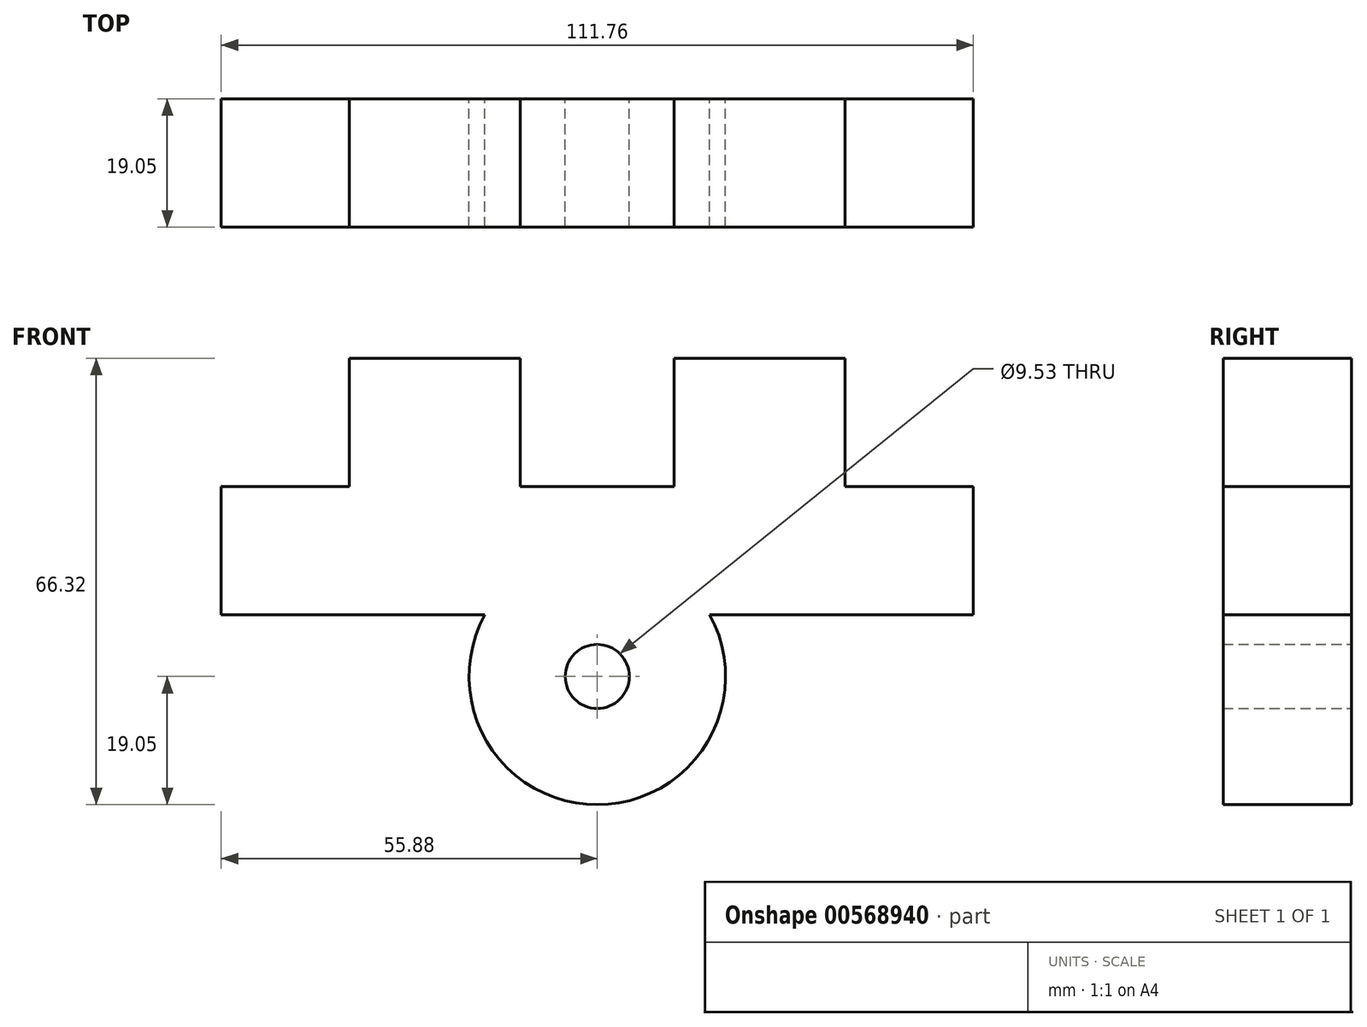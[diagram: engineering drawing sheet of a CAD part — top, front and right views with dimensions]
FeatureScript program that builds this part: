
annotation { "Feature Type Name" : "Feature", "Feature Type Description" : "" }
export const myFeature = defineFeature(function(context is Context, id is Id, definition is map)
    precondition{}
    {
        {
            var Q0;
            Q0=qCreatedBy(makeId("Front.planeOp"),FACE);
            var sketch = newSketch(context, id + "F0", { "sketchPlane" : qUnion([Q0])});
            skCircle(sketch, "E0", {"center": v(0, 0) * mm, "radius": 19.05 * mm});
            skLineSegment(sketch, "E1", {"start": v(0, 0) * mm, "end": v(0, 19.05) * mm});
            skCircle(sketch, "E2", {"center": v(0, 0) * mm, "radius": 4.76 * mm});
            skLineSegment(sketch, "E3.bottom", {"start": v(-55.88, 28.22) * mm, "end": v(55.88, 28.22) * mm});
            skLineSegment(sketch, "E3.top", {"start": v(-55.88, 9.17) * mm, "end": v(55.88, 9.17) * mm});
            skLineSegment(sketch, "E3.left", {"start": v(-55.88, 28.22) * mm, "end": v(-55.88, 9.17) * mm});
            skLineSegment(sketch, "E3.right", {"start": v(55.88, 28.22) * mm, "end": v(55.88, 9.17) * mm});
            skLineSegment(sketch, "E4.bottom", {"start": v(-36.83, 28.22) * mm, "end": v(-11.43, 28.22) * mm});
            skLineSegment(sketch, "E4.top", {"start": v(-36.83, 47.27) * mm, "end": v(-11.43, 47.27) * mm});
            skLineSegment(sketch, "E4.left", {"start": v(-36.83, 28.22) * mm, "end": v(-36.83, 47.27) * mm});
            skLineSegment(sketch, "E4.right", {"start": v(-11.43, 28.22) * mm, "end": v(-11.43, 47.27) * mm});
            skLineSegment(sketch, "E5.bottom", {"start": v(11.43, 28.22) * mm, "end": v(36.83, 28.22) * mm});
            skLineSegment(sketch, "E5.top", {"start": v(11.43, 47.27) * mm, "end": v(36.83, 47.27) * mm});
            skLineSegment(sketch, "E5.left", {"start": v(11.43, 28.22) * mm, "end": v(11.43, 47.27) * mm});
            skLineSegment(sketch, "E5.right", {"start": v(36.83, 28.22) * mm, "end": v(36.83, 47.27) * mm});
            skSolve(sketch);
        }
        {
            var Q0;
            Q0 = qSketchRegion(id + "F0", true);
            extrude(context, id + "F1", {"entities" : qUnion([Q0]), "depth" : 19.05 * mm, "offsetDistance" : 25.4 * mm});
        }
    });
